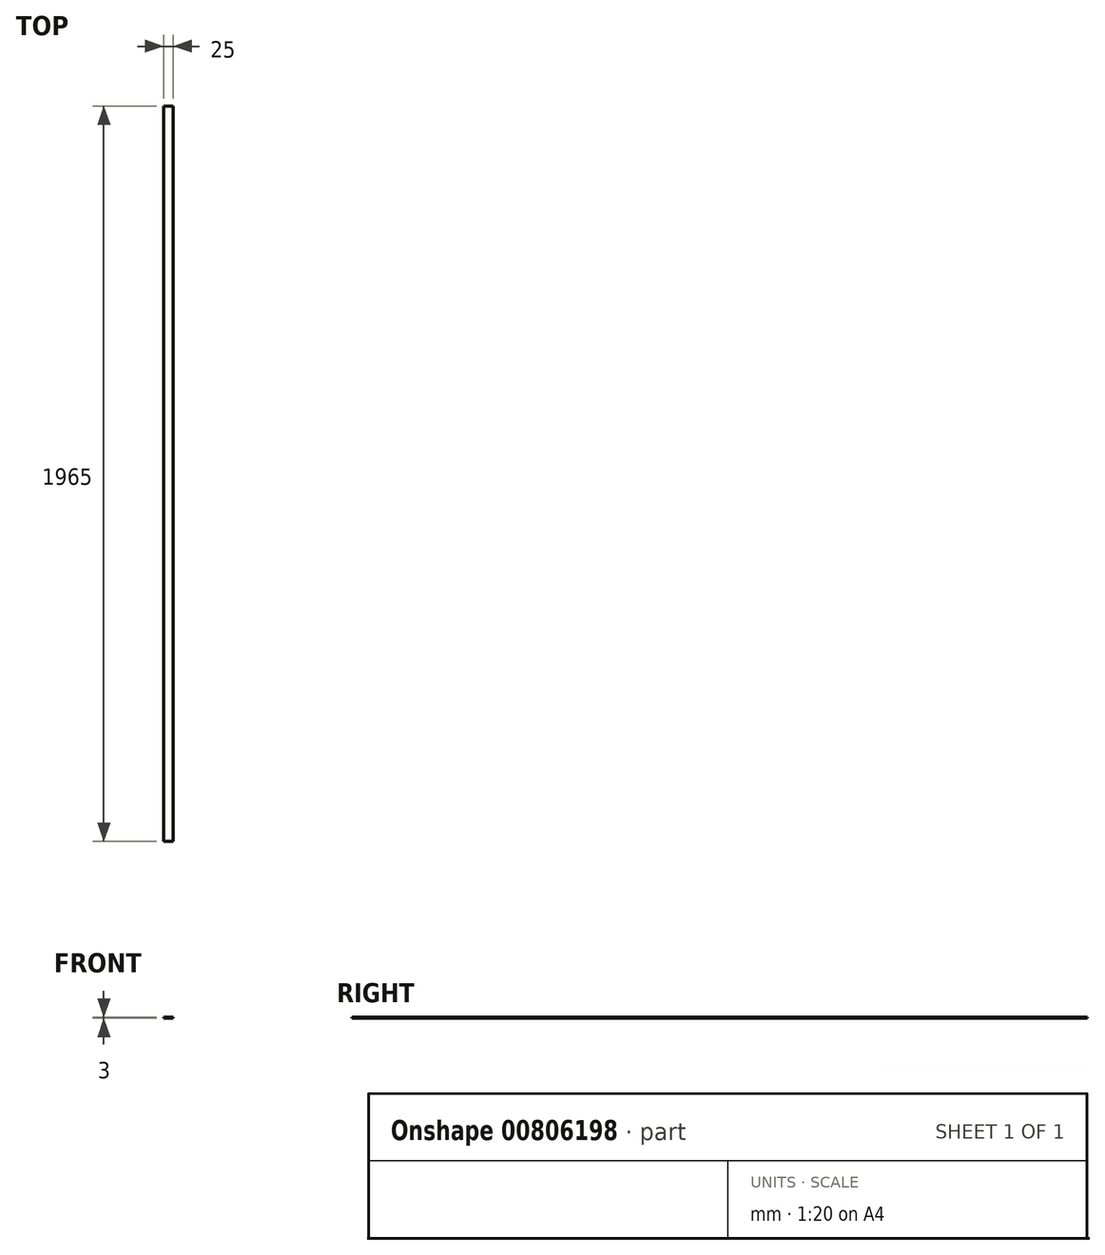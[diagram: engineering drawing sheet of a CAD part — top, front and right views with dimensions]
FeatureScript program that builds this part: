
annotation { "Feature Type Name" : "Feature", "Feature Type Description" : "" }
export const myFeature = defineFeature(function(context is Context, id is Id, definition is map)
    precondition{}
    {
        {
            var Q0;
            Q0=qCreatedBy(makeId("Front.planeOp"),FACE);
            var sketch = newSketch(context, id + "F0", { "sketchPlane" : qUnion([Q0])});
            skLineSegment(sketch, "E0.bottom", {"start": v(0, 0) * mm, "end": v(25, 0) * mm});
            skLineSegment(sketch, "E0.top", {"start": v(0, -3) * mm, "end": v(25, -3) * mm});
            skLineSegment(sketch, "E0.left", {"start": v(0, 0) * mm, "end": v(0, -3) * mm});
            skLineSegment(sketch, "E0.right", {"start": v(25, 0) * mm, "end": v(25, -3) * mm});
            skSolve(sketch);
        }
        {
            var Q0;
            Q0=qSketchRegion(id+"F0",true);
            extrude(context, id + "F1", {"entities" : qUnion([Q0]), "depth" : 1965 * mm, "offsetDistance" : 25 * mm});
        }
    });
